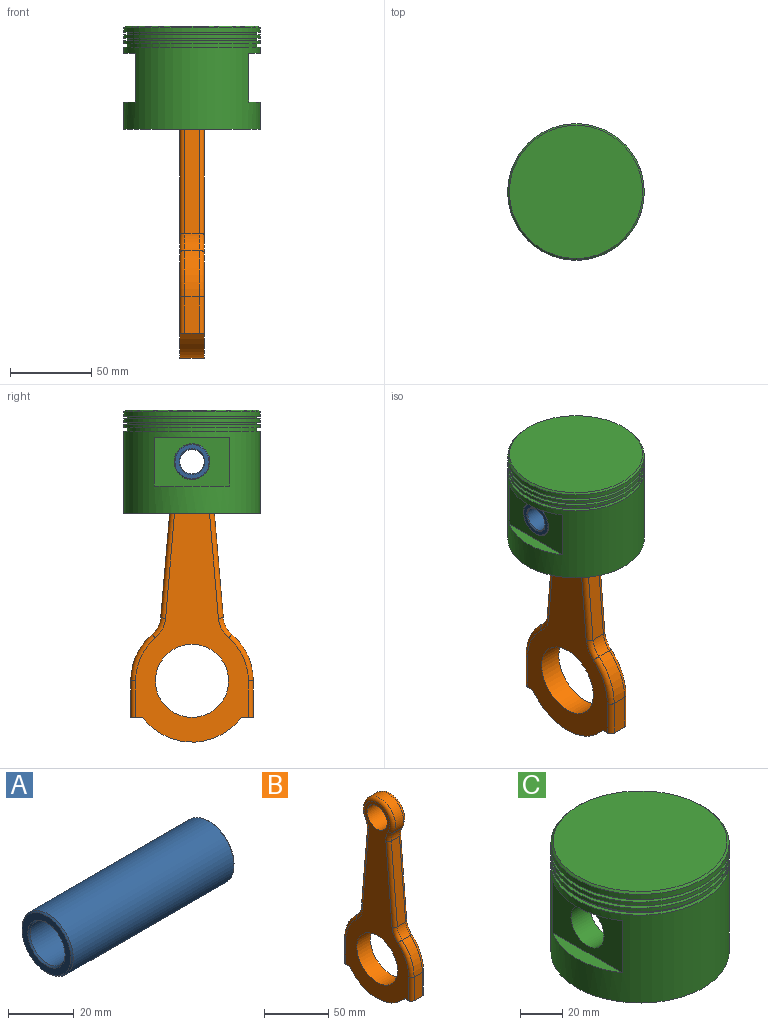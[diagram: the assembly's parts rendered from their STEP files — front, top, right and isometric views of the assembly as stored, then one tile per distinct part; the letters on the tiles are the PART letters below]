
ASSEMBLY  parts=3 mates=2
PART A: 8 faces, bbox 70x22x22 mm
  f0: cylinder r=7.5mm len=69mm, axis (-1,0,0), area 3251.5mm2, adj f4,f6
  f1: cylinder r=11mm len=69mm, axis (-1,0,0), area 4768.9mm2, adj f5,f7
  f2: plane 21x21mm, normal (1,0,0), area 145.3mm2, adj f6,f7
  f3: plane 21x21mm, normal (-1,0,0), area 145.3mm2, adj f4,f5
  f4: cone r=8mm half-angle=45deg, axis (-1,0,0), area 34.4mm2, adj f0,f3
  f5: cone r=11mm half-angle=45deg, axis (1,0,0), area 47.8mm2, adj f1,f3
  f6: cone r=7.5mm half-angle=45deg, axis (1,0,0), area 34.4mm2, adj f0,f2
  f7: cone r=10.5mm half-angle=45deg, axis (-1,0,0), area 47.8mm2, adj f1,f2
PART B: 40 faces, bbox 15x81.7x191.1 mm
  f0: cylinder r=37.72mm len=28.71mm, axis (-1,0,0), area 293.6mm2, adj f1,f17,f19,f30
  f1: plane 22.5x9mm, normal (0,-1,0), area 202.5mm2, adj f0,f2,f18,f29
  f2: plane 15x7.45mm, normal (0,0,-1), area 107.8mm2, adj f1,f3,f12,f13,f18,f29
  f3: cylinder r=37.72mm len=60.56mm, axis (-1,0,0), area 1054.4mm2, adj f2,f4,f12,f13
  f4: plane 15x7.45mm, normal (0,0,-1), area 107.8mm2, adj f3,f5,f12,f13,f28,f39
  f5: plane 22.5x9mm, normal (0,1,0), area 202.5mm2, adj f4,f6,f28,f39
  f6: cylinder r=37.72mm len=28.71mm, axis (-1,0,0), area 293.6mm2, adj f5,f14,f27,f38
  f7: plane 78.51x9mm, normal (0,1,0.09), area 709.2mm2, adj f14,f15,f25,f36
  f8: cylinder r=17mm len=34mm, axis (-1,0,0), area 645mm2, adj f15,f16,f23,f34
  f9: cylinder r=22.5mm len=45mm, axis (-1,0,0), area 2120.6mm2, adj f12,f13
  f10: cylinder r=11mm len=22mm, axis (-1,0,0), area 1036.7mm2, adj f12,f13
  f11: plane 78.51x9mm, normal (0,-1,0.09), area 709.2mm2, adj f16,f17,f21,f32
  f12: plane 186.72x69.45mm, normal (1,0,0), area 5068mm2, adj f2,f3,f4,f9,f10,f29,f30,f31
  f13: plane 186.72x69.45mm, normal (-1,0,0), area 5068mm2, adj f2,f3,f4,f9,f10,f18,f19,f20
  f14: cylinder r=15mm len=10.14mm, axis (-1,0,0), area 105.2mm2, adj f6,f7,f26,f37
  f15: cylinder r=15mm len=9mm, axis (-1,0,0), area 84mm2, adj f7,f8,f24,f35
  f16: cylinder r=15mm len=9mm, axis (-1,0,0), area 84mm2, adj f8,f11,f22,f33
  f17: cylinder r=15mm len=10.14mm, axis (-1,0,0), area 105.2mm2, adj f0,f11,f20,f31
  f18: cylinder r=3mm len=22.5mm, axis (0,0,-1), area 106mm2, adj f1,f2,f13,f19
  f19: torus R=34.72mm, axis (1,0,0), area 149.3mm2, adj f0,f13,f18,f20
  f20: torus R=18mm, axis (1,0,0), area 59.1mm2, adj f13,f17,f19,f21
  f21: cylinder r=3mm len=78.76mm, axis (0,-0.09,-1), area 371.3mm2, adj f11,f13,f20,f22
  f22: torus R=18mm, axis (1,0,0), area 47.2mm2, adj f13,f16,f21,f23
  f23: torus R=14mm, axis (1,0,0), area 316.1mm2, adj f8,f13,f22,f24
  f24: torus R=18mm, axis (1,0,0), area 47.2mm2, adj f13,f15,f23,f25
  f25: cylinder r=3mm len=78.76mm, axis (0,-0.09,1), area 371.3mm2, adj f7,f13,f24,f26
  f26: torus R=18mm, axis (1,0,0), area 59.1mm2, adj f13,f14,f25,f27
  f27: torus R=34.72mm, axis (1,0,0), area 149.3mm2, adj f6,f13,f26,f28
  f28: cylinder r=3mm len=22.5mm, axis (0,0,1), area 106mm2, adj f4,f5,f13,f27
  f29: cylinder r=3mm len=22.5mm, axis (0,0,1), area 106mm2, adj f1,f2,f12,f30
  f30: torus R=34.72mm, axis (1,0,0), area 149.3mm2, adj f0,f12,f29,f31
  f31: torus R=18mm, axis (1,0,0), area 59.1mm2, adj f12,f17,f30,f32
  f32: cylinder r=3mm len=78.76mm, axis (0,0.09,1), area 371.3mm2, adj f11,f12,f31,f33
  f33: torus R=18mm, axis (1,0,0), area 47.2mm2, adj f12,f16,f32,f34
  f34: torus R=14mm, axis (1,0,0), area 316.1mm2, adj f8,f12,f33,f35
  f35: torus R=18mm, axis (1,0,0), area 47.2mm2, adj f12,f15,f34,f36
  f36: cylinder r=3mm len=78.76mm, axis (0,0.09,-1), area 371.3mm2, adj f7,f12,f35,f37
  f37: torus R=18mm, axis (1,0,0), area 59.1mm2, adj f12,f14,f36,f38
  f38: torus R=34.72mm, axis (1,0,0), area 149.3mm2, adj f6,f12,f37,f39
  f39: cylinder r=3mm len=22.5mm, axis (0,0,-1), area 106mm2, adj f4,f5,f12,f38
PART C: 29 faces, bbox 84x84x63.6 mm
  f0: cylinder r=42mm len=84mm, axis (0,0,-1), area 10411.7mm2, adj f14,f16,f23,f24,f25,f26,f27,f28
  f1: cylinder r=11mm len=22mm, axis (1,0,0), area 863.9mm2, adj f18,f25
  f2: cylinder r=42mm len=84mm, axis (0,0,-1), area 791.7mm2, adj f4,f5
  f3: plane 82x82mm, normal (0,0,1), area 5281mm2, adj f4
  f4: cone r=41mm half-angle=45deg, axis (0,0,-1), area 368.8mm2, adj f2,f3
  f5: plane 84x84mm, normal (0,0,-1), area 515.2mm2, adj f2,f7
  f6: plane 84x84mm, normal (0,0,1), area 515.2mm2, adj f7,f8
  f7: cylinder r=40mm len=80mm, axis (0,0,1), area 377mm2, adj f5,f6
  f8: cylinder r=42mm len=84mm, axis (0,0,-1), area 527.8mm2, adj f6,f9
  f9: plane 84x84mm, normal (0,0,-1), area 515.2mm2, adj f8,f11
  f10: plane 84x84mm, normal (0,0,1), area 515.2mm2, adj f11,f12
  f11: cylinder r=40mm len=80mm, axis (0,0,1), area 377mm2, adj f9,f10
  f12: cylinder r=42mm len=84mm, axis (0,0,-1), area 527.8mm2, adj f10,f13
  f13: plane 84x84mm, normal (0,0,-1), area 515.2mm2, adj f12,f15
  f14: plane 84x84mm, normal (0,0,1), area 515.2mm2, adj f0,f15
  f15: cylinder r=40mm len=80mm, axis (0,0,1), area 502.7mm2, adj f13,f14
  f16: plane 84x84mm, normal (0,0,-1), area 2333.7mm2, adj f0,f17,f18,f19,f20
  f17: cylinder r=38mm len=59.52mm, axis (0,0,-1), area 2866.4mm2, adj f16,f18,f19,f21
  f18: plane 61.25x59.52mm, normal (1,0,0), area 3265.2mm2, adj f1,f16,f17,f20,f21
  f19: plane 61.25x59.52mm, normal (-1,0,0), area 3265.2mm2, adj f16,f17,f20,f21,f22
  f20: cylinder r=38mm len=59.52mm, axis (0,0,-1), area 2866.4mm2, adj f16,f18,f19,f21
  f21: plane 76x45mm, normal (0,0,-1), area 3208.1mm2, adj f17,f18,f19,f20
  f22: cylinder r=11mm len=22mm, axis (1,0,0), area 863.9mm2, adj f19,f28
  f23: plane 46.43x7mm, normal (0,0,-1), area 220.6mm2, adj f0,f25
  f24: plane 46.43x7mm, normal (0,0,1), area 220.6mm2, adj f0,f25
  f25: plane 46.43x30mm, normal (-1,0,0), area 1012.8mm2, adj f0,f1,f23,f24
  f26: plane 46.43x7mm, normal (0,0,-1), area 220.6mm2, adj f0,f28
  f27: plane 46.43x7mm, normal (0,0,1), area 220.6mm2, adj f0,f28
  f28: plane 46.43x30mm, normal (1,0,0), area 1012.8mm2, adj f0,f22,f26,f27
PLACE A at identity
PLACE B t=(0,0,-135)mm
PLACE C at identity fixed
MATE fastened A.f1 <-> C.f1  axis (1,0,0) through (35,0,0)mm
MATE revolute B.f10 <-> A.f1  axis (-1,0,0) through (0,0,0)mm
